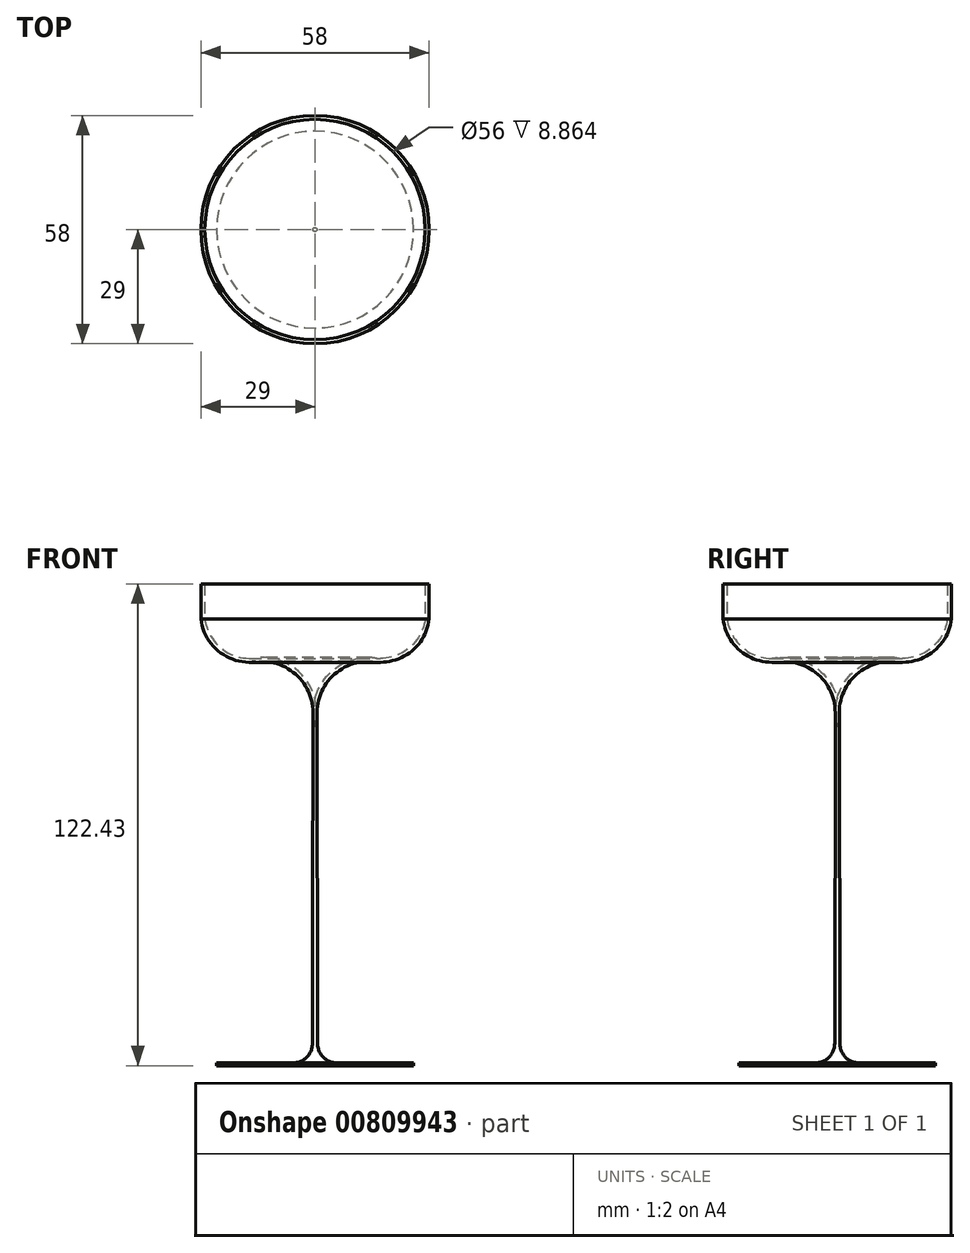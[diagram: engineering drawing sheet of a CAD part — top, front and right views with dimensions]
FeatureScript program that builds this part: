
annotation { "Feature Type Name" : "Feature", "Feature Type Description" : "" }
export const myFeature = defineFeature(function(context is Context, id is Id, definition is map)
    precondition{}
    {
        {
            var Q0;
            Q0=qCreatedBy(makeId("Front.planeOp"),FACE);
            var sketch = newSketch(context, id + "F0", { "sketchPlane" : qUnion([Q0])});
            skLineSegment(sketch, "E0", {"start": v(-25, -121.76) * mm, "end": v(-25, -122.43) * mm});
            skLineSegment(sketch, "E1", {"start": v(-25, -122.43) * mm, "end": v(0, -122.43) * mm});
            skLineSegment(sketch, "E2", {"start": v(-5.65, -121.76) * mm, "end": v(-25, -121.76) * mm});
            skLineSegment(sketch, "E3", {"start": v(-0.5, -32.76) * mm, "end": v(-0.65, -116.77) * mm});
            skLineSegment(sketch, "E4", {"start": v(0, -33.43) * mm, "end": v(0, -122.43) * mm});
            skArc(sketch, "E5", {"start": v(-15.08, -19.85) * mm, "mid": v(-4.88, -23.01) * mm, "end": v(-0.5, -32.76) * mm});
            skArc(sketch, "E6", {"start": v(-15.08, -19.85) * mm, "mid": v(-24.31, -17.28) * mm, "end": v(-29, -8.92) * mm});
            skLineSegment(sketch, "E7", {"start": v(-29, -8.92) * mm, "end": v(-29, 0) * mm});
            skLineSegment(sketch, "E8.0", {"start": v(-28, -8.86) * mm, "end": v(-28, 0) * mm});
            skArc(sketch, "E8.1", {"start": v(-15.2, -18.85) * mm, "mid": v(-23.67, -16.5) * mm, "end": v(-28, -8.86) * mm});
            skArc(sketch, "E8.2", {"start": v(-15.2, -18.85) * mm, "mid": v(-5.7, -21.12) * mm, "end": v(0, -29.06) * mm});
            skLineSegment(sketch, "E9", {"start": v(-29, 0) * mm, "end": v(-28, 0) * mm});
            skLineSegment(sketch, "E10", {"start": v(0, -33.43) * mm, "end": v(0, -29.06) * mm});
            skPoint(sketch, "E11.visualSharp", {"position": v(-0.66, -121.76) * mm});
            skArc(sketch, "E11.filletArc", {"start": v(-5.65, -121.76) * mm, "mid": v(-2.12, -120.3) * mm, "end": v(-0.65, -116.77) * mm});
            skSolve(sketch);
        }
        {
            var Q0;
            Q0=makeQuery(id+"F0.imprint","IMPRINT",FACE,{"disambiguationData":[TD([[makeQuery(id+"F0.imprint","IMPRINT",EDGE,{"derivedFrom":sQuery(id+"F0.wireOp",EDGE,"E0")}),1.0]])]});
            var Q1;
            Q1=sQuery(id+"F0.wireOp",EDGE,"E4");
            revolve(context, id + "F1", {"surfaceOperationType" : NewSurfaceOperationType.NEW, "entities" : qUnion([Q0]), "axis" : qUnion([Q1]), "revolveType" : RevolveType.FULL, "oppositeDirection" : true});
        }
    });
